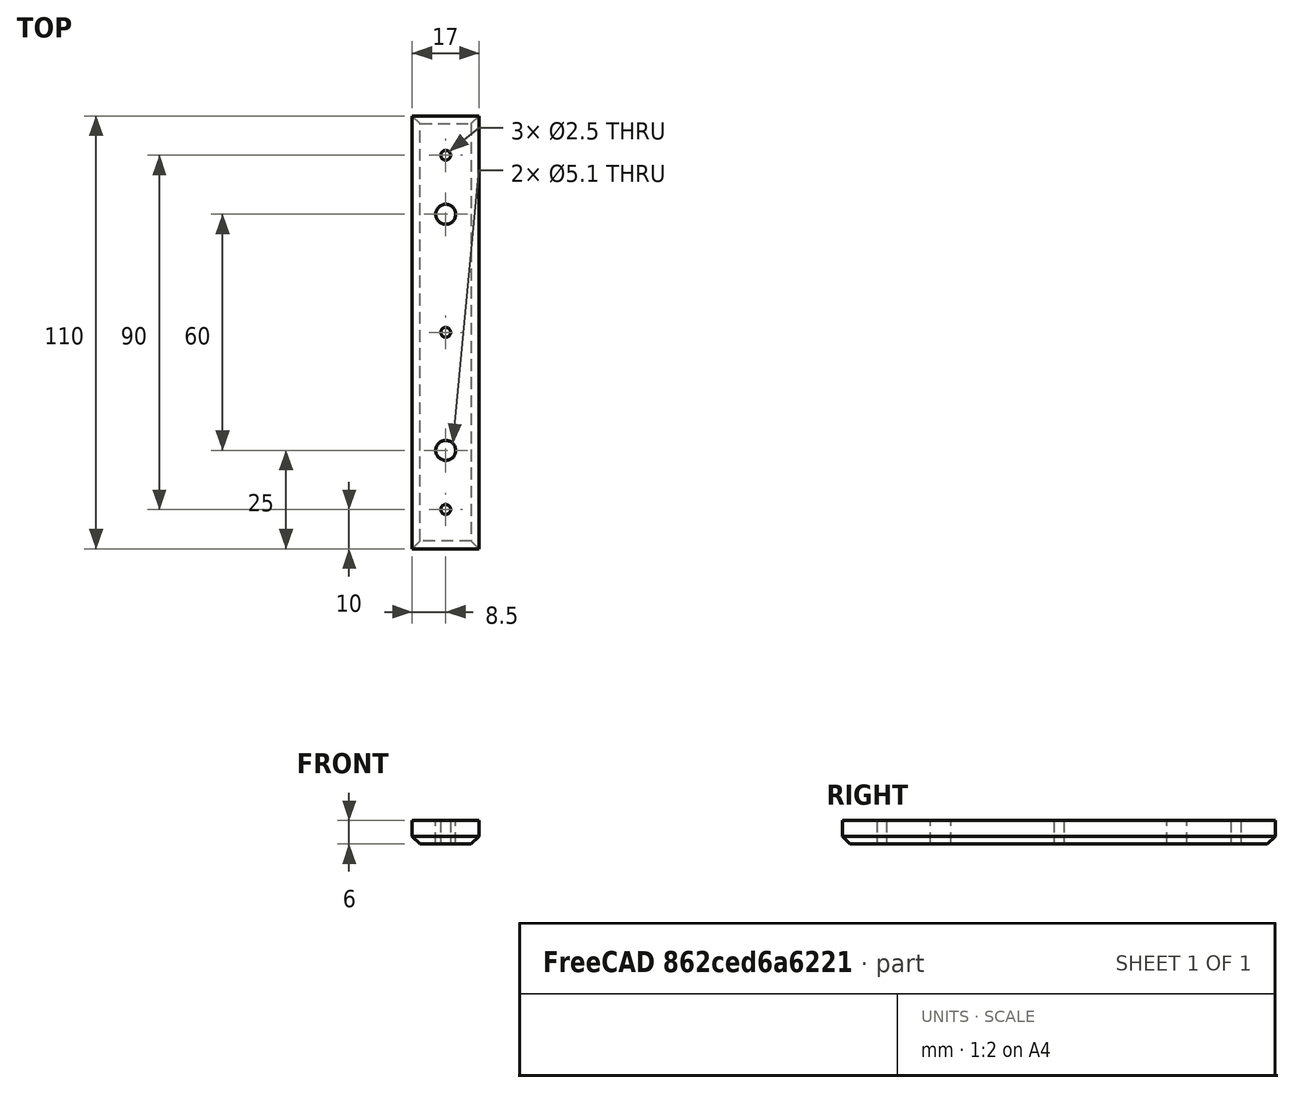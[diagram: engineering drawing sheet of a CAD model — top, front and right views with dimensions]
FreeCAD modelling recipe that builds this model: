
FCSTD DOCUMENT  (FreeCAD 0.20R29603 (Git))
Label: Tube Block
License: All rights reserved
LicenseURL: https://en.wikipedia.org/wiki/All_rights_reserved
objects: TechDraw::DrawViewDimension×8, Sketcher::SketchObject×3, PartDesign::Hole×2, TechDraw::DrawProjGroupItem×2, PartDesign::Pad×1, TechDraw::DrawSVGTemplate×1, PartDesign::Chamfer×1, PartDesign::Body×1, TechDraw::DrawProjGroup×1, TechDraw::DrawPage×1
note: 12 computed .brp shape members not serialized (recipe doc carries the construction recipe); baked Part::Feature solids carry a one-line shape summary decoded from their .brp

FEATURE [Sketcher::SketchObject] Sketch
  FullyConstrained = true
  MapMode = 5
  Support = -> [XY_Plane]
  sketch-geometry (5):
    g0: LineSegment StartX=-8.5 StartY=-55 StartZ=0 EndX=-8.5 EndY=55 EndZ=0
    g1: LineSegment StartX=-8.5 StartY=55 StartZ=0 EndX=8.5 EndY=55 EndZ=0
    g2: LineSegment StartX=8.5 StartY=55 StartZ=0 EndX=8.5 EndY=-55 EndZ=0
    g3: LineSegment StartX=8.5 StartY=-55 StartZ=0 EndX=-8.5 EndY=-55 EndZ=0
    g4: GeomPoint X=0 Y=0 Z=0
  constraints (12):
    c: Coincident(g0,g1)
    c: Coincident(g1,g2)
    c: Coincident(g2,g3)
    c: Coincident(g3,g0)
    c: Horizontal(g1)
    c: Horizontal(g3)
    c: Vertical(g0)
    c: Vertical(g2)
    c: Symmetric(g1,g0,g4)
    c: Coincident(g4,g-1)
    c: DistanceX(g1,g1) = 17
    c: DistanceY(g2,g2) = 110
FEATURE [PartDesign::Pad] Pad
  AlongSketchNormal = false
  Direction = (0,0,1)
  Length = 6
  Length2 = 10
  Profile = -> Sketch
  ReferenceAxis = -> Sketch [N_Axis]
  Type = 0
FEATURE [Sketcher::SketchObject] Sketch001
  FullyConstrained = true
  MapMode = 5
  Support = -> [XY_Plane]
  sketch-geometry (2):
    g0: Circle CenterX=0 CenterY=30 CenterZ=0 NormalX=0 NormalY=0 NormalZ=1 AngleXU=0 Radius=3.175
    g1: Circle CenterX=0 CenterY=-30 CenterZ=0 NormalX=0 NormalY=0 NormalZ=1 AngleXU=0 Radius=3.175
  constraints (5):
    c: PointOnObject(g0,g-2)
    c: Symmetric(g0,g1,g-1)
    c: DistanceY(g1,g0) = 60
    c: Diameter(g0) = 6.35
    c: Equal(g1,g0)
FEATURE [Sketcher::SketchObject] Sketch002
  FullyConstrained = true
  MapMode = 5
  Placement = pos=(0,0,6) rot=(0,0,1;0rad)
  Support = -> [Pad]
  sketch-geometry (3):
    g0: Circle CenterX=0 CenterY=45 CenterZ=0 NormalX=0 NormalY=0 NormalZ=1 AngleXU=0 Radius=1.4
    g1: Circle CenterX=0 CenterY=-45 CenterZ=0 NormalX=0 NormalY=0 NormalZ=1 AngleXU=0 Radius=1.4
    g2: Circle CenterX=0 CenterY=0 CenterZ=0 NormalX=0 NormalY=0 NormalZ=1 AngleXU=0 Radius=1.4
  constraints (7):
    c: PointOnObject(g0,g-2)
    c: Equal(g0,g1)
    c: Diameter(g0) = 2.8
    c: Symmetric(g0,g1,g-1)
    c: Coincident(g2,g-1)
    c: Equal(g1,g2)
    c: DistanceY(g1,g0) = 90
FEATURE [PartDesign::Hole] Hole
  BaseFeature = -> Pad
  CustomThreadClearance = 0
  Depth = 6
  DepthType = 0
  Diameter = 5.1
  DrillForDepth = false
  DrillPoint = 0
  DrillPointAngle = 118
  HoleCutCountersinkAngle = 90
  HoleCutCustomValues = false
  HoleCutDepth = 0
  HoleCutDiameter = 6.1
  HoleCutType = 0
  ModelThread = false
  Profile = -> Sketch001
  Reversed = true
  Tapered = false
  TaperedAngle = 90
  ThreadClass = 0
  ThreadDepth = 6
  ThreadDepthType = 0
  ThreadDirection = 0
  ThreadFit = 0
  ThreadSize = 9
  ThreadType = 3
  Threaded = true
  UseCustomThreadClearance = false
FEATURE [PartDesign::Hole] Hole001
  BaseFeature = -> Hole
  CustomThreadClearance = 0
  Depth = 6
  DepthType = 0
  Diameter = 2.5
  DrillForDepth = false
  DrillPoint = 0
  DrillPointAngle = 118
  HoleCutCountersinkAngle = 90
  HoleCutCustomValues = false
  HoleCutDepth = 0
  HoleCutDiameter = 6.1
  HoleCutType = 0
  ModelThread = false
  Profile = -> Sketch002
  Tapered = false
  TaperedAngle = 90
  ThreadClass = 0
  ThreadDepth = 6
  ThreadDepthType = 0
  ThreadDirection = 0
  ThreadFit = 0
  ThreadSize = 9
  ThreadType = 1
  Threaded = true
  UseCustomThreadClearance = false
FEATURE [TechDraw::DrawSVGTemplate] Template
  Height = 297
  Orientation = 1
  Width = 420
FEATURE [PartDesign::Chamfer] Chamfer
  Angle = 45
  Base = -> Hole001 [Edge6,Edge9,Edge3,Edge11]
  BaseFeature = -> Hole001
  ChamferType = 0
  FlipDirection = false
  Size = 2
  Size2 = 1
  SupportTransform = false
  UseAllEdges = false
FEATURE [PartDesign::Body] Body  label="Tube Block"
  Group = -> [Sketch,Pad,Sketch001,Sketch002,Hole,Hole001,Chamfer]
  Origin = -> Origin
  Tip = -> Chamfer
FEATURE [TechDraw::DrawProjGroupItem] ProjItem  label="Top"
  CoarseView = false
  Direction = (0,0,-1)
  Focus = 100
  HardHidden = false
  IsoCount = 0
  IsoHidden = false
  IsoVisible = false
  LockPosition = true
  Perspective = false
  Rotation = 0
  RotationVector = (0,-1,0)
  ScaleType = 2
  SeamHidden = false
  SeamVisible = true
  SmoothHidden = false
  SmoothVisible = true
  Source = -> [Body]
  Type = 0
  X = 0
  XDirection = (0,-1,0)
  Y = 0
FEATURE [TechDraw::DrawProjGroupItem] ProjItem001  label="Front"
  CoarseView = false
  Direction = (1,0,0)
  Focus = 100
  HardHidden = false
  IsoCount = 0
  IsoHidden = false
  IsoVisible = false
  LockPosition = false
  Perspective = false
  Rotation = 0
  RotationVector = (1,0,0)
  ScaleType = 2
  SeamHidden = false
  SeamVisible = true
  SmoothHidden = false
  SmoothVisible = true
  Source = -> [Body]
  Type = 5
  X = 0
  XDirection = (0,-1,0)
  Y = 72.3846
FEATURE [TechDraw::DrawProjGroup] ProjGroup
  Anchor = -> ProjItem
  AutoDistribute = false
  LockPosition = false
  ProjectionType = 0
  Rotation = 0
  ScaleType = 0
  Source = -> [Body]
  Views = -> [ProjItem,ProjItem001]
  X = 213.735
  Y = 145.714
  spacingX = 15
  spacingY = 15
FEATURE [TechDraw::DrawViewDimension] Dimension
  AngleOverride = false
  Arbitrary = true
  ArbitraryTolerances = false
  EqualTolerance = true
  ExtensionAngle = 0
  FormatSpec = 3X M3 THRU
  FormatSpecOverTolerance = %+.2w
  FormatSpecUnderTolerance = %+.2w
  Inverted = false
  LineAngle = 0
  LockPosition = false
  MeasureType = 1
  OverTolerance = 0
  References2D = -> [ProjItem]
  Rotation = 0
  ScaleType = 0
  TheoreticalExact = false
  Type = 5
  UnderTolerance = 0
  X = -79.6866
  Y = -26.7455
FEATURE [TechDraw::DrawViewDimension] Dimension001
  AngleOverride = false
  Arbitrary = true
  ArbitraryTolerances = false
  EqualTolerance = true
  ExtensionAngle = 0
  FormatSpec = 2X ⌀1/4-20 THRU
  FormatSpecOverTolerance = %+.2w
  FormatSpecUnderTolerance = %+.2w
  Inverted = false
  LineAngle = 0
  LockPosition = false
  MeasureType = 1
  OverTolerance = 0
  References2D = -> [ProjItem]
  Rotation = 0
  ScaleType = 0
  TheoreticalExact = false
  Type = 5
  UnderTolerance = 0
  X = -73.2437
  Y = -41.3734
FEATURE [TechDraw::DrawViewDimension] Dimension002
  AngleOverride = false
  Arbitrary = false
  ArbitraryTolerances = false
  EqualTolerance = true
  ExtensionAngle = 0
  FormatSpec = %.2w
  FormatSpecOverTolerance = %+.2w
  FormatSpecUnderTolerance = %+.2w
  Inverted = false
  LineAngle = 0
  LockPosition = false
  MeasureType = 1
  OverTolerance = 0
  References2D = -> [ProjItem001]
  Rotation = 0
  ScaleType = 0
  TheoreticalExact = false
  Type = 1
  UnderTolerance = 0
  X = 1.40766
  Y = -19.5034
FEATURE [TechDraw::DrawViewDimension] Dimension003
  AngleOverride = false
  Arbitrary = false
  ArbitraryTolerances = false
  EqualTolerance = true
  ExtensionAngle = 0
  FormatSpec = %.2w
  FormatSpecOverTolerance = %+.2w
  FormatSpecUnderTolerance = %+.2w
  Inverted = false
  LineAngle = 0
  LockPosition = false
  MeasureType = 1
  OverTolerance = 0
  References2D = -> [ProjItem]
  Rotation = 0
  ScaleType = 0
  TheoreticalExact = false
  Type = 2
  UnderTolerance = 0
  X = 75.2703
  Y = 23.6149
FEATURE [TechDraw::DrawViewDimension] Dimension004
  AngleOverride = false
  Arbitrary = false
  ArbitraryTolerances = false
  EqualTolerance = true
  ExtensionAngle = 0
  FormatSpec = %.2w
  FormatSpecOverTolerance = %+.2w
  FormatSpecUnderTolerance = %+.2w
  Inverted = false
  LineAngle = 0
  LockPosition = false
  MeasureType = 1
  OverTolerance = 0
  References2D = -> [ProjItem001]
  Rotation = 0
  ScaleType = 0
  TheoreticalExact = false
  Type = 2
  UnderTolerance = 0
  X = 73.7072
  Y = 21.0811
FEATURE [TechDraw::DrawViewDimension] Dimension005
  AngleOverride = false
  Arbitrary = false
  ArbitraryTolerances = false
  EqualTolerance = true
  ExtensionAngle = 0
  FormatSpec = %.2w
  FormatSpecOverTolerance = %+.2w
  FormatSpecUnderTolerance = %+.2w
  Inverted = false
  LineAngle = 0
  LockPosition = false
  MeasureType = 1
  OverTolerance = 0
  References2D = -> [ProjItem001]
  Rotation = 0
  ScaleType = 0
  TheoreticalExact = false
  Type = 2
  UnderTolerance = 0
  X = -70.1905
  Y = 18.8576
FEATURE [TechDraw::DrawViewDimension] Dimension006
  AngleOverride = false
  Arbitrary = false
  ArbitraryTolerances = false
  EqualTolerance = true
  ExtensionAngle = 0
  FormatSpec = %.2w
  FormatSpecOverTolerance = %+.2w
  FormatSpecUnderTolerance = %+.2w
  Inverted = false
  LineAngle = 0
  LockPosition = false
  MeasureType = 1
  OverTolerance = 0
  References2D = -> [ProjItem]
  Rotation = 0
  ScaleType = 0
  TheoreticalExact = false
  Type = 1
  UnderTolerance = 0
  X = -16.2948
  Y = 23.0729
FEATURE [TechDraw::DrawViewDimension] Dimension007
  AngleOverride = false
  Arbitrary = false
  ArbitraryTolerances = false
  EqualTolerance = true
  ExtensionAngle = 0
  FormatSpec = %.2w
  FormatSpecOverTolerance = %+.2w
  FormatSpecUnderTolerance = %+.2w
  Inverted = false
  LineAngle = 0
  LockPosition = false
  MeasureType = 1
  OverTolerance = 0
  References2D = -> [ProjItem]
  Rotation = 0
  ScaleType = 0
  TheoreticalExact = false
  Type = 1
  UnderTolerance = 0
  X = -23.6509
  Y = 37.4596
FEATURE [TechDraw::DrawPage] Page
  KeepUpdated = true
  NextBalloonIndex = 1
  ProjectionType = 0
  Template = -> Template
  Views = -> [ProjGroup,Dimension,Dimension001,Dimension002,Dimension003,Dimension004,Dimension005,Dimension006,Dimension007]
